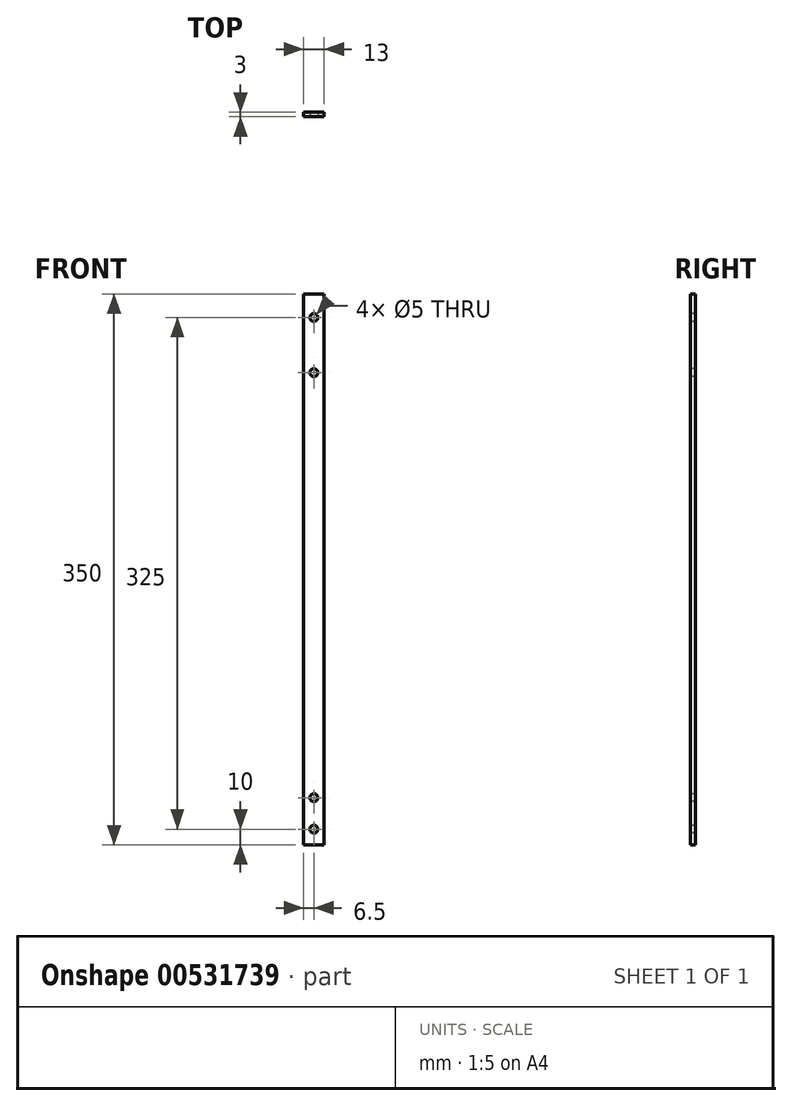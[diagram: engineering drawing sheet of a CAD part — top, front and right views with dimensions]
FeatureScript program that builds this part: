
annotation { "Feature Type Name" : "Feature", "Feature Type Description" : "" }
export const myFeature = defineFeature(function(context is Context, id is Id, definition is map)
    precondition{}
    {
        {
            var Q0;
            Q0=qCreatedBy(makeId("Front.planeOp"),FACE);
            var sketch = newSketch(context, id + "F0", { "sketchPlane" : qUnion([Q0])});
            skLineSegment(sketch, "E0.bottom", {"start": v(6.5, 175) * mm, "end": v(-6.5, 175) * mm});
            skLineSegment(sketch, "E0.top", {"start": v(6.5, -175) * mm, "end": v(-6.5, -175) * mm});
            skLineSegment(sketch, "E0.left", {"start": v(6.5, 175) * mm, "end": v(6.5, -175) * mm});
            skLineSegment(sketch, "E0.right", {"start": v(-6.5, 175) * mm, "end": v(-6.5, -175) * mm});
            skPoint(sketch, "E0.middle", {"position": v(0, 0) * mm});
            skSolve(sketch);
        }
        {
            var Q0;
            Q0=makeQuery(id+"F0.imprint","IMPRINT",FACE,{"disambiguationData":[TD([[makeQuery(id+"F0.imprint","IMPRINT",EDGE,{"derivedFrom":sQuery(id+"F0.wireOp",EDGE,"E0.bottom")}),1.0]])]});
            extrude(context, id + "F1", {"entities" : qUnion([Q0]), "depth" : 3 * mm, "offsetDistance" : 25 * mm});
        }
        {
            var Q0;
            Q0=makeQuery(id+"F1.opExtrude","CAP_FACE",FACE,{"disambiguationData":[OSD([sQuery(id+"F0.wireOp",EDGE,"E0.bottom"),sQuery(id+"F0.wireOp",EDGE,"E0.top"),sQuery(id+"F0.wireOp",EDGE,"E0.left"),sQuery(id+"F0.wireOp",EDGE,"E0.right")])],"isStart":false});
            var sketch = newSketch(context, id + "F2", { "sketchPlane" : qUnion([Q0])});
            skLineSegment(sketch, "E1", {"start": v(0, 175) * mm, "end": v(0, 160) * mm});
            skCircle(sketch, "E2", {"center": v(0, 160) * mm, "radius": 2.5 * mm});
            skSolve(sketch);
        }
        {
            var Q0;
            Q0=makeQuery(id+"F2.imprint","IMPRINT",FACE,{"disambiguationData":[TD([[makeQuery(id+"F2.imprint","IMPRINT",EDGE,{"derivedFrom":sQuery(id+"F2.wireOp",EDGE,"E2")}),1.0]])]});
            extrude(context, id + "F3", {"entities" : qUnion([Q0]), "operationType" : NewBodyOperationType.REMOVE, "oppositeDirection" : true, "depth" : 3 * mm, "offsetDistance" : 25 * mm});
        }
        {
            var Q0;
            Q0=makeQuery(id+"F1.opExtrude","CAP_FACE",FACE,{"disambiguationData":[OSD([sQuery(id+"F0.wireOp",EDGE,"E0.bottom"),sQuery(id+"F0.wireOp",EDGE,"E0.top"),sQuery(id+"F0.wireOp",EDGE,"E0.left"),sQuery(id+"F0.wireOp",EDGE,"E0.right")])],"isStart":false});
            var sketch = newSketch(context, id + "F4", { "sketchPlane" : qUnion([Q0])});
            skLineSegment(sketch, "E3", {"start": v(0, -175) * mm, "end": v(0, -165) * mm});
            skPoint(sketch, "E3.endSnap0", {"position": v(0, -175) * mm});
            skCircle(sketch, "E4", {"center": v(0, -165) * mm, "radius": 2.5 * mm});
            skLineSegment(sketch, "E5", {"start": v(0, -165) * mm, "end": v(0, -145) * mm});
            skCircle(sketch, "E6", {"center": v(0, -145) * mm, "radius": 2.5 * mm});
            skSolve(sketch);
        }
        {
            var Q0;
            Q0=makeQuery(id+"F4.imprint","IMPRINT",FACE,{"disambiguationData":[TD([[makeQuery(id+"F4.imprint","IMPRINT",EDGE,{"derivedFrom":sQuery(id+"F4.wireOp",EDGE,"78aXldw9-ysBR-KM8a-f9kw-b8tRlMLRAOFC")}),1.0]])]});
            var Q1;
            {var subQ0=sQuery(id+"F4.wireOp",EDGE,"asxdFDqv-kU0y-VXVM-JVxb-IH92wcDA4mLB");var subQ1=sQuery(id+"F4.wireOp",EDGE,"E3");var subQ2=makeQuery(id+"F4.imprint","INTERSECT",VERTEX,{"derivedFrom":[subQ1,subQ0]});Q1=makeQuery(id+"F4.imprint","IMPRINT",FACE,{"disambiguationData":[TD([[makeQuery(id+"F4.imprint","IMPRINT",EDGE,{"disambiguationData":[TD([[subQ2,1.0]])],"derivedFrom":subQ1}),1.0]])]});}
            var Q2;
            {var subQ0=sQuery(id+"F4.wireOp",EDGE,"asxdFDqv-kU0y-VXVM-JVxb-IH92wcDA4mLB");var subQ1=sQuery(id+"F4.wireOp",EDGE,"E3");var subQ2=makeQuery(id+"F4.imprint","INTERSECT",VERTEX,{"derivedFrom":[subQ1,subQ0]});Q2=makeQuery(id+"F4.imprint","IMPRINT",FACE,{"disambiguationData":[TD([[makeQuery(id+"F4.imprint","IMPRINT",EDGE,{"disambiguationData":[TD([[subQ2,1.0]])],"derivedFrom":subQ1}),-1.0]])]});}
            extrude(context, id + "F5", {"entities" : qUnion([Q0, Q1, Q2]), "operationType" : NewBodyOperationType.REMOVE, "oppositeDirection" : true, "depth" : 25 * mm, "offsetDistance" : 25 * mm});
        }
        {
            var Q0;
            Q0=makeQuery(id+"F1.opExtrude","CAP_FACE",FACE,{"disambiguationData":[OSD([sQuery(id+"F0.wireOp",EDGE,"E0.bottom"),sQuery(id+"F0.wireOp",EDGE,"E0.top"),sQuery(id+"F0.wireOp",EDGE,"E0.left"),sQuery(id+"F0.wireOp",EDGE,"E0.right")])],"isStart":false});
            var sketch = newSketch(context, id + "F6", { "sketchPlane" : qUnion([Q0])});
            skLineSegment(sketch, "E7", {"start": v(0, 175) * mm, "end": v(0, 125) * mm});
            skCircle(sketch, "E8", {"center": v(0, 125) * mm, "radius": 2.5 * mm});
            skSolve(sketch);
        }
        {
            var Q0;
            Q0=makeQuery(id+"F6.imprint","IMPRINT",FACE,{"disambiguationData":[TD([[makeQuery(id+"F6.imprint","IMPRINT",EDGE,{"derivedFrom":sQuery(id+"F6.wireOp",EDGE,"E8")}),1.0]])]});
            extrude(context, id + "F7", {"entities" : qUnion([Q0]), "operationType" : NewBodyOperationType.REMOVE, "oppositeDirection" : true, "depth" : 25 * mm, "offsetDistance" : 25 * mm});
        }
        {
            var Q0;
            Q0 = qSketchRegion(id + "F4", true);
            extrude(context, id + "F8", {"entities" : qUnion([Q0]), "operationType" : NewBodyOperationType.REMOVE, "oppositeDirection" : true, "depth" : 25 * mm, "offsetDistance" : 25 * mm});
        }
    });
